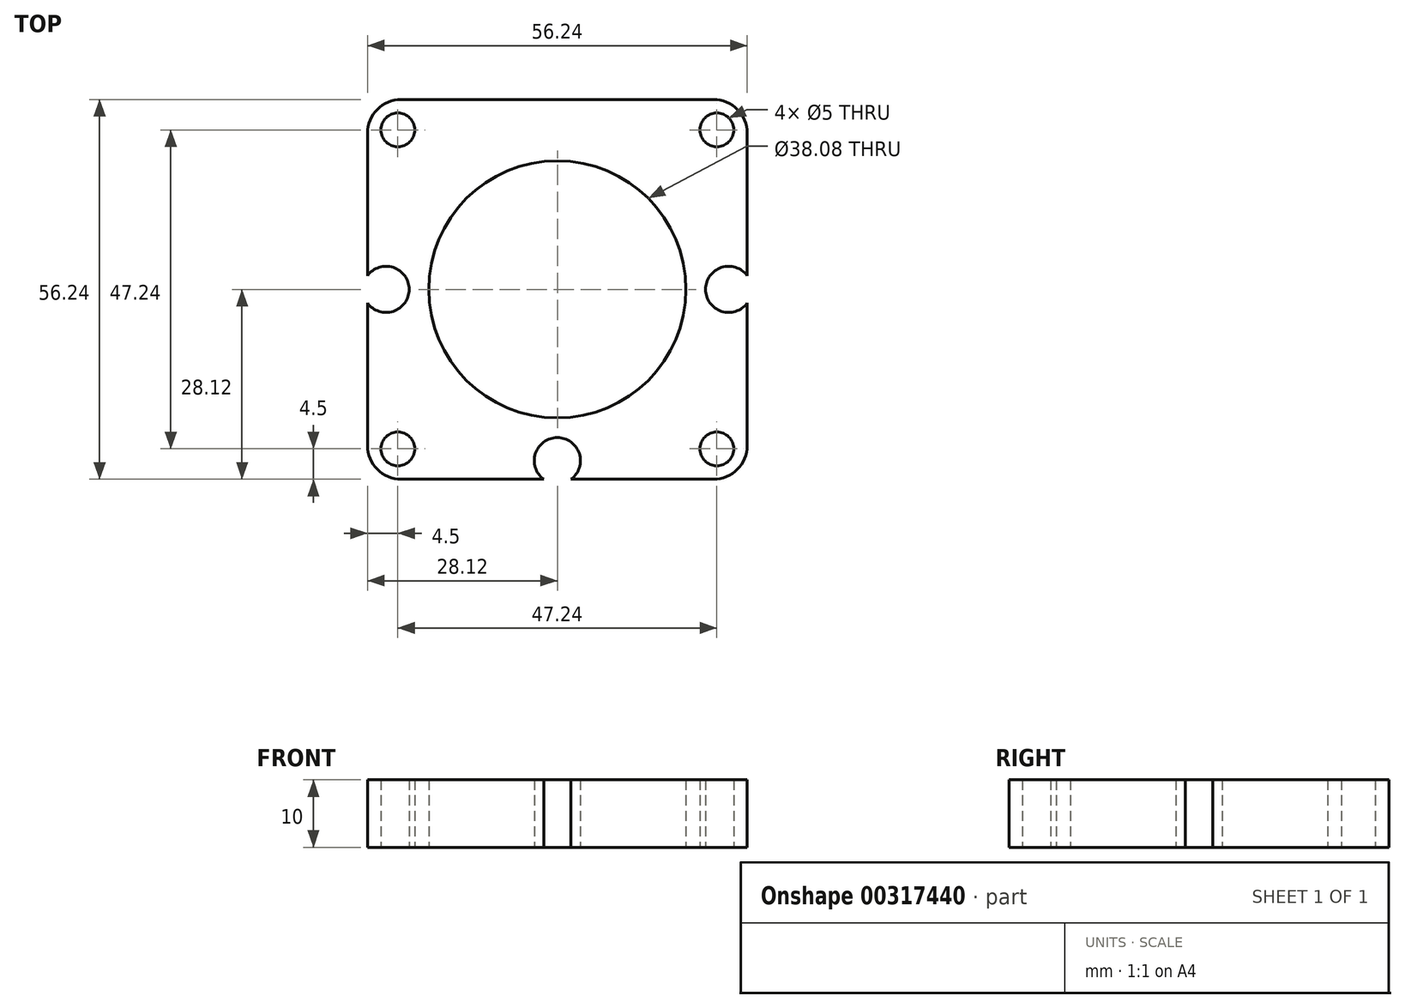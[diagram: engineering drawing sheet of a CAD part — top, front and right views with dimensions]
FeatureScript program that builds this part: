
annotation { "Feature Type Name" : "Feature", "Feature Type Description" : "" }
export const myFeature = defineFeature(function(context is Context, id is Id, definition is map)
    precondition{}
    {
        {
            var Q0;
            Q0=qCreatedBy(makeId("Top.planeOp"),FACE);
            var sketch = newSketch(context, id + "F0", { "sketchPlane" : qUnion([Q0])});
            skLineSegment(sketch, "E0.rect.bottom", {"start": v(-28.11, 28.11) * mm, "end": v(28.12, 28.11) * mm});
            skLineSegment(sketch, "E0.rect.top", {"start": v(-28.11, -28.11) * mm, "end": v(28.11, -28.11) * mm});
            skLineSegment(sketch, "E0.rect.left", {"start": v(-28.11, 28.12) * mm, "end": v(-28.12, -28.11) * mm});
            skLineSegment(sketch, "E0.rect.right", {"start": v(28.12, 28.12) * mm, "end": v(28.11, -28.11) * mm});
            skPoint(sketch, "E0.rect.middle", {"position": v(0, 0) * mm});
            skCircle(sketch, "E1", {"center": v(0, 0) * mm, "radius": 19.04 * mm});
            skCircle(sketch, "E2", {"center": v(0, 0) * mm, "radius": 3.98 * mm});
            skCircle(sketch, "E3", {"center": v(-23.62, 23.62) * mm, "radius": 2.5 * mm});
            skCircle(sketch, "E4", {"center": v(23.62, 23.62) * mm, "radius": 2.5 * mm});
            skCircle(sketch, "E5", {"center": v(23.62, -23.62) * mm, "radius": 2.5 * mm});
            skCircle(sketch, "E6", {"center": v(-23.62, -23.62) * mm, "radius": 2.5 * mm});
            skLineSegment(sketch, "E7.rect.bottom", {"start": v(-23.62, 23.62) * mm, "end": v(23.62, 23.62) * mm, "construction": true});
            skLineSegment(sketch, "E7.rect.top", {"start": v(-23.62, -23.62) * mm, "end": v(23.62, -23.62) * mm, "construction": true});
            skLineSegment(sketch, "E7.rect.left", {"start": v(-23.62, 23.62) * mm, "end": v(-23.62, -23.62) * mm, "construction": true});
            skLineSegment(sketch, "E7.rect.right", {"start": v(23.62, 23.62) * mm, "end": v(23.62, -23.62) * mm, "construction": true});
            skCircle(sketch, "E8", {"center": v(0, 0) * mm, "radius": 5.38 * mm});
            skCircle(sketch, "E9", {"center": v(-25.37, 0) * mm, "radius": 8.13 * mm});
            skCircle(sketch, "E10", {"center": v(25.37, 0) * mm, "radius": 8.13 * mm});
            skCircle(sketch, "E11", {"center": v(0, -25.37) * mm, "radius": 8.13 * mm});
            skCircle(sketch, "E12", {"center": v(-25.37, 0) * mm, "radius": 3.42 * mm});
            skCircle(sketch, "E13", {"center": v(25.37, 0) * mm, "radius": 3.41 * mm});
            skCircle(sketch, "E14", {"center": v(0, -25.37) * mm, "radius": 3.42 * mm});
            skSolve(sketch);
        }
        {
            var Q0;
            {var subQ6=sQuery(id+"F0.wireOp",EDGE,"E0.rect.bottom");Q0=makeQuery(id+"F0.imprint","IMPRINT",FACE,{"disambiguationData":[TD([[makeQuery(id+"F0.imprint","IMPRINT",EDGE,{"derivedFrom":subQ6}),-1.0]])]});}
            var Q1;
            {var subQ0=sQuery(id+"F0.wireOp",EDGE,"E9");var subQ1=sQuery(id+"F0.wireOp",EDGE,"E0.rect.left");var subQ2=makeQuery(id+"F0.imprint","INTERSECT",VERTEX,{"disambiguationData":[OD(0.0)],"derivedFrom":[subQ1,subQ0]});Q1=makeQuery(id+"F0.imprint","IMPRINT",FACE,{"disambiguationData":[TD([[makeQuery(id+"F0.imprint","IMPRINT",EDGE,{"disambiguationData":[TD([[subQ2,-1.0]])],"derivedFrom":subQ1}),1.0]])]});}
            var Q2;
            {var subQ0=sQuery(id+"F0.wireOp",EDGE,"E12");var subQ1=sQuery(id+"F0.wireOp",EDGE,"E0.rect.left");var subQ2=makeQuery(id+"F0.imprint","INTERSECT",VERTEX,{"disambiguationData":[OD(0.0)],"derivedFrom":[subQ1,subQ0]});Q2=makeQuery(id+"F0.imprint","IMPRINT",FACE,{"disambiguationData":[TD([[makeQuery(id+"F0.imprint","IMPRINT",EDGE,{"disambiguationData":[TD([[subQ2,-1.0]])],"derivedFrom":subQ1}),1.0]])]});}
            var Q3;
            Q3=makeQuery(id+"F0.imprint","IMPRINT",FACE,{"disambiguationData":[TD([[makeQuery(id+"F0.imprint","IMPRINT",EDGE,{"derivedFrom":sQuery(id+"F0.wireOp",EDGE,"E6")}),-1.0]])]});
            var Q4;
            {var subQ0=sQuery(id+"F0.wireOp",EDGE,"E11");var subQ1=sQuery(id+"F0.wireOp",EDGE,"E0.rect.top");var subQ2=makeQuery(id+"F0.imprint","INTERSECT",VERTEX,{"disambiguationData":[OD(0.0)],"derivedFrom":[subQ1,subQ0]});Q4=makeQuery(id+"F0.imprint","IMPRINT",FACE,{"disambiguationData":[TD([[makeQuery(id+"F0.imprint","IMPRINT",EDGE,{"disambiguationData":[TD([[subQ2,-1.0]])],"derivedFrom":subQ1}),1.0]])]});}
            var Q5;
            {var subQ0=sQuery(id+"F0.wireOp",EDGE,"E14");var subQ1=sQuery(id+"F0.wireOp",EDGE,"E0.rect.top");var subQ2=makeQuery(id+"F0.imprint","INTERSECT",VERTEX,{"disambiguationData":[OD(0.0)],"derivedFrom":[subQ1,subQ0]});Q5=makeQuery(id+"F0.imprint","IMPRINT",FACE,{"disambiguationData":[TD([[makeQuery(id+"F0.imprint","IMPRINT",EDGE,{"disambiguationData":[TD([[subQ2,-1.0]])],"derivedFrom":subQ1}),1.0]])]});}
            var Q6;
            Q6=makeQuery(id+"F0.imprint","IMPRINT",FACE,{"disambiguationData":[TD([[makeQuery(id+"F0.imprint","IMPRINT",EDGE,{"derivedFrom":sQuery(id+"F0.wireOp",EDGE,"E5")}),-1.0]])]});
            var Q7;
            {var subQ0=sQuery(id+"F0.wireOp",EDGE,"E10");var subQ1=sQuery(id+"F0.wireOp",EDGE,"E0.rect.right");var subQ2=makeQuery(id+"F0.imprint","INTERSECT",VERTEX,{"disambiguationData":[OD(0.0)],"derivedFrom":[subQ1,subQ0]});Q7=makeQuery(id+"F0.imprint","IMPRINT",FACE,{"disambiguationData":[TD([[makeQuery(id+"F0.imprint","IMPRINT",EDGE,{"disambiguationData":[TD([[subQ2,-1.0]])],"derivedFrom":subQ1}),-1.0]])]});}
            var Q8;
            {var subQ0=sQuery(id+"F0.wireOp",EDGE,"E13");var subQ1=sQuery(id+"F0.wireOp",EDGE,"E0.rect.right");var subQ2=makeQuery(id+"F0.imprint","INTERSECT",VERTEX,{"disambiguationData":[OD(0.0)],"derivedFrom":[subQ1,subQ0]});Q8=makeQuery(id+"F0.imprint","IMPRINT",FACE,{"disambiguationData":[TD([[makeQuery(id+"F0.imprint","IMPRINT",EDGE,{"disambiguationData":[TD([[subQ2,-1.0]])],"derivedFrom":subQ1}),-1.0]])]});}
            extrude(context, id + "F1", {"entities" : qUnion([Q0, Q1, Q2, Q3, Q4, Q5, Q6, Q7, Q8]), "depth" : 79 * mm, "hasSecondDirection" : true, "secondDirectionOppositeDirection" : false, "secondDirectionDepth" : 69 * mm});
        }
        {
            var Q0;
            Q0=makeQuery(id+"F1.opExtrude","SWEPT_EDGE",EDGE,{"disambiguationData":[OSD([sQuery(id+"F0.wireOp",EDGE,"E0.rect.top"),sQuery(id+"F0.wireOp",EDGE,"E0.rect.left")])]});
            var Q1;
            Q1=makeQuery(id+"F1.opExtrude","SWEPT_EDGE",EDGE,{"disambiguationData":[OSD([sQuery(id+"F0.wireOp",EDGE,"E0.rect.bottom"),sQuery(id+"F0.wireOp",EDGE,"E0.rect.left")])]});
            var Q2;
            Q2=makeQuery(id+"F1.opExtrude","SWEPT_EDGE",EDGE,{"disambiguationData":[OSD([sQuery(id+"F0.wireOp",EDGE,"E0.rect.bottom"),sQuery(id+"F0.wireOp",EDGE,"E0.rect.right")])]});
            var Q3;
            Q3=makeQuery(id+"F1.opExtrude","SWEPT_EDGE",EDGE,{"disambiguationData":[OSD([sQuery(id+"F0.wireOp",EDGE,"E0.rect.top"),sQuery(id+"F0.wireOp",EDGE,"E0.rect.right")])]});
            fillet(context, id + "F2", {"entities" : qUnion([Q0, Q1, Q2, Q3]), "radius" : 5 * mm, "tangentPropagation" : true, "allowEdgeOverflow" : false});
        }
    });
